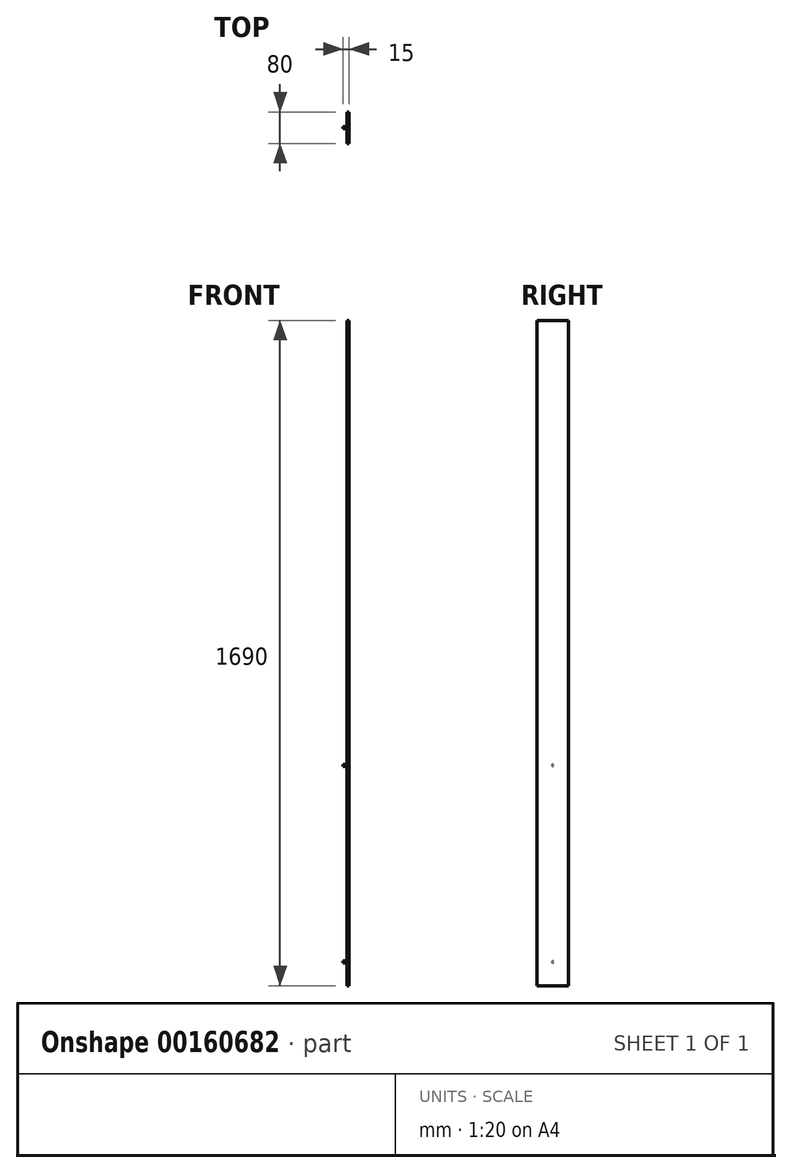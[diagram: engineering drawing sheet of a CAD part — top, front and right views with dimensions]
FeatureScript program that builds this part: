
annotation { "Feature Type Name" : "Feature", "Feature Type Description" : "" }
export const myFeature = defineFeature(function(context is Context, id is Id, definition is map)
    precondition{}
    {
        {
            var Q0;
            Q0=qCreatedBy(makeId("Right.planeOp"),FACE);
            var sketch = newSketch(context, id + "F0", { "sketchPlane" : qUnion([Q0])});
            skLineSegment(sketch, "E0.bottom", {"start": v(-40, 845) * mm, "end": v(40, 845) * mm});
            skLineSegment(sketch, "E0.top", {"start": v(-40, -845) * mm, "end": v(40, -845) * mm});
            skLineSegment(sketch, "E0.left", {"start": v(-40, 845) * mm, "end": v(-40, -845) * mm});
            skLineSegment(sketch, "E0.right", {"start": v(40, 845) * mm, "end": v(40, -845) * mm});
            skSolve(sketch);
        }
        {
            var Q0;
            Q0=makeQuery(id+"F0.imprint","IMPRINT",FACE,{"disambiguationData":[TD([[makeQuery(id+"F0.imprint","IMPRINT",EDGE,{"derivedFrom":sQuery(id+"F0.wireOp",EDGE,"E0.bottom")}),-1.0]])]});
            extrude(context, id + "F1", {"entities" : qUnion([Q0]), "depth" : 15 * mm});
        }
        {
            var Q0;
            Q0=makeQuery(id+"F1.opExtrude","CAP_FACE",FACE,{"disambiguationData":[OSD([sQuery(id+"F0.wireOp",EDGE,"E0.bottom"),sQuery(id+"F0.wireOp",EDGE,"E0.top"),sQuery(id+"F0.wireOp",EDGE,"E0.left"),sQuery(id+"F0.wireOp",EDGE,"E0.right")])],"isStart":true});
            var sketch = newSketch(context, id + "F2", { "sketchPlane" : qUnion([Q0])});
            skCircle(sketch, "E1", {"center": v(0, 785) * mm, "radius": 2.5 * mm});
            skCircle(sketch, "E2", {"center": v(0, 285) * mm, "radius": 2.5 * mm});
            skCircle(sketch, "E3.MirrorC", {"center": v(0, -785) * mm, "radius": 2.5 * mm});
            skCircle(sketch, "E4.MirrorC", {"center": v(0, -285) * mm, "radius": 2.5 * mm});
            skSolve(sketch);
        }
        {
            var Q0;
            Q0=makeQuery(id+"F2.imprint","IMPRINT",FACE,{"disambiguationData":[TD([[makeQuery(id+"F2.imprint","IMPRINT",EDGE,{"derivedFrom":sQuery(id+"F2.wireOp",EDGE,"E1")}),1.0]])]});
            var Q1;
            Q1=makeQuery(id+"F2.imprint","IMPRINT",FACE,{"disambiguationData":[TD([[makeQuery(id+"F2.imprint","IMPRINT",EDGE,{"derivedFrom":sQuery(id+"F2.wireOp",EDGE,"E2")}),1.0]])]});
            var Q2;
            Q2=makeQuery(id+"F2.imprint","IMPRINT",FACE,{"disambiguationData":[TD([[makeQuery(id+"F2.imprint","IMPRINT",EDGE,{"derivedFrom":sQuery(id+"F2.wireOp",EDGE,"E4.MirrorC")}),-1.0]])]});
            var Q3;
            Q3=makeQuery(id+"F2.imprint","IMPRINT",FACE,{"disambiguationData":[TD([[makeQuery(id+"F2.imprint","IMPRINT",EDGE,{"derivedFrom":sQuery(id+"F2.wireOp",EDGE,"E3.MirrorC")}),-1.0]])]});
            extrude(context, id + "F3", {"entities" : qUnion([Q0, Q1, Q2, Q3]), "operationType" : NewBodyOperationType.REMOVE, "oppositeDirection" : true, "depth" : 10 * mm});
        }
    });
